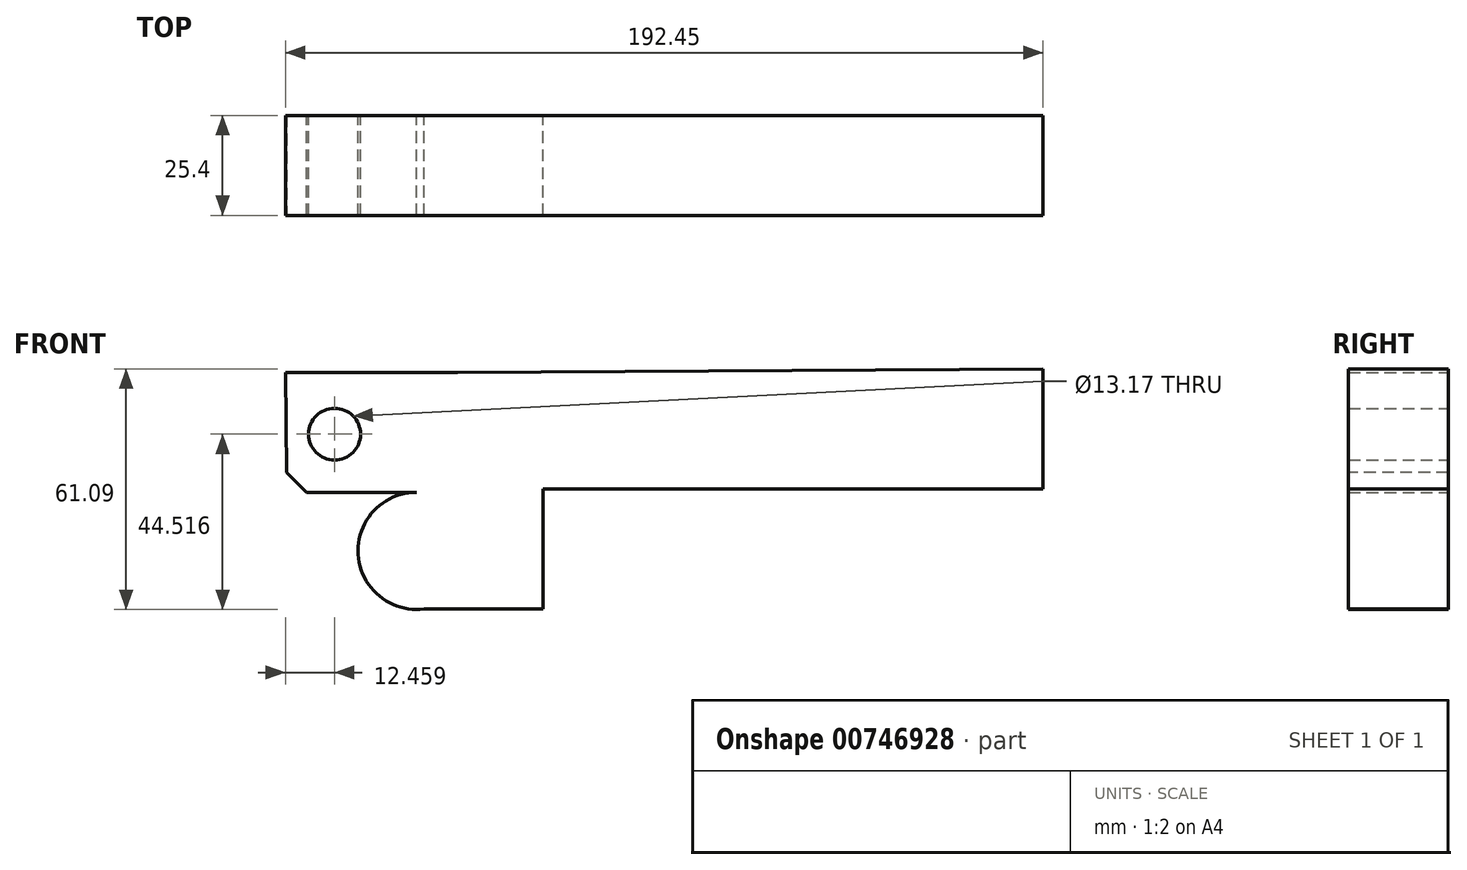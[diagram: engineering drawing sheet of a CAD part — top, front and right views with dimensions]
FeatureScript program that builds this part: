
annotation { "Feature Type Name" : "Feature", "Feature Type Description" : "" }
export const myFeature = defineFeature(function(context is Context, id is Id, definition is map)
    precondition{}
    {
        {
            var Q0;
            Q0=qCreatedBy(makeId("Front.planeOp"),FACE);
            var sketch = newSketch(context, id + "F0", { "sketchPlane" : qUnion([Q0])});
            skLineSegment(sketch, "E0", {"start": v(91.06, 43) * mm, "end": v(91.06, 12.53) * mm});
            skLineSegment(sketch, "E1", {"start": v(91.06, 12.53) * mm, "end": v(-35.94, 12.53) * mm});
            skLineSegment(sketch, "E2", {"start": v(-35.94, 12.53) * mm, "end": v(-35.94, -17.95) * mm});
            skLineSegment(sketch, "E3", {"start": v(-35.94, -17.95) * mm, "end": v(-66.18, -17.95) * mm});
            skLineSegment(sketch, "E4", {"start": v(-68.1, 11.69) * mm, "end": v(-101.11, 11.69) * mm});
            skLineSegment(sketch, "E5", {"start": v(-101.11, 11.69) * mm, "end": v(-101.39, 42.17) * mm});
            skLineSegment(sketch, "E6", {"start": v(-101.39, 42.17) * mm, "end": v(-57.65, 42.17) * mm});
            skArc(sketch, "E7", {"start": v(-68.1, 11.69) * mm, "mid": v(-82.94, -4.15) * mm, "end": v(-66.18, -17.95) * mm});
            skLineSegment(sketch, "E8", {"start": v(-57.65, 42.17) * mm, "end": v(91.06, 43) * mm});
            skCircle(sketch, "E9", {"center": v(-88.93, 26.44) * mm, "radius": 6.59 * mm});
            skSolve(sketch);
        }
        {
            var Q0;
            Q0 = qSketchRegion(id + "F0", true);
            extrude(context, id + "F1", {"entities" : qUnion([Q0]), "depth" : 21.08 * mm, "offsetDistance" : 25.4 * mm});
        }
        {
            var Q0;
            Q0 = qSketchRegion(id + "F0", true);
            extrude(context, id + "F2", {"entities" : qUnion([Q0]), "operationType" : NewBodyOperationType.ADD, "depth" : 25.4 * mm, "offsetDistance" : 25.4 * mm});
        }
        {
            var Q0;
            {var subQ0=sQuery(id+"F0.wireOp",EDGE,"E5");var subQ1=sQuery(id+"F0.wireOp",EDGE,"E4");Q0=makeQuery(id+"F2.boolean.opBoolean","MERGE",EDGE,{"derivedFrom":[makeQuery(id+"F1.opExtrude","SWEPT_EDGE",EDGE,{"disambiguationData":[OSD([subQ1,subQ0])]}),makeQuery(id+"F2.opExtrude","SWEPT_EDGE",EDGE,{"disambiguationData":[OSD([subQ1,subQ0])]})]});}
            chamfer(context, id + "F3", {"entities" : qUnion([Q0]), "width" : 5.08 * mm, "tangentPropagation" : true});
        }
    });
